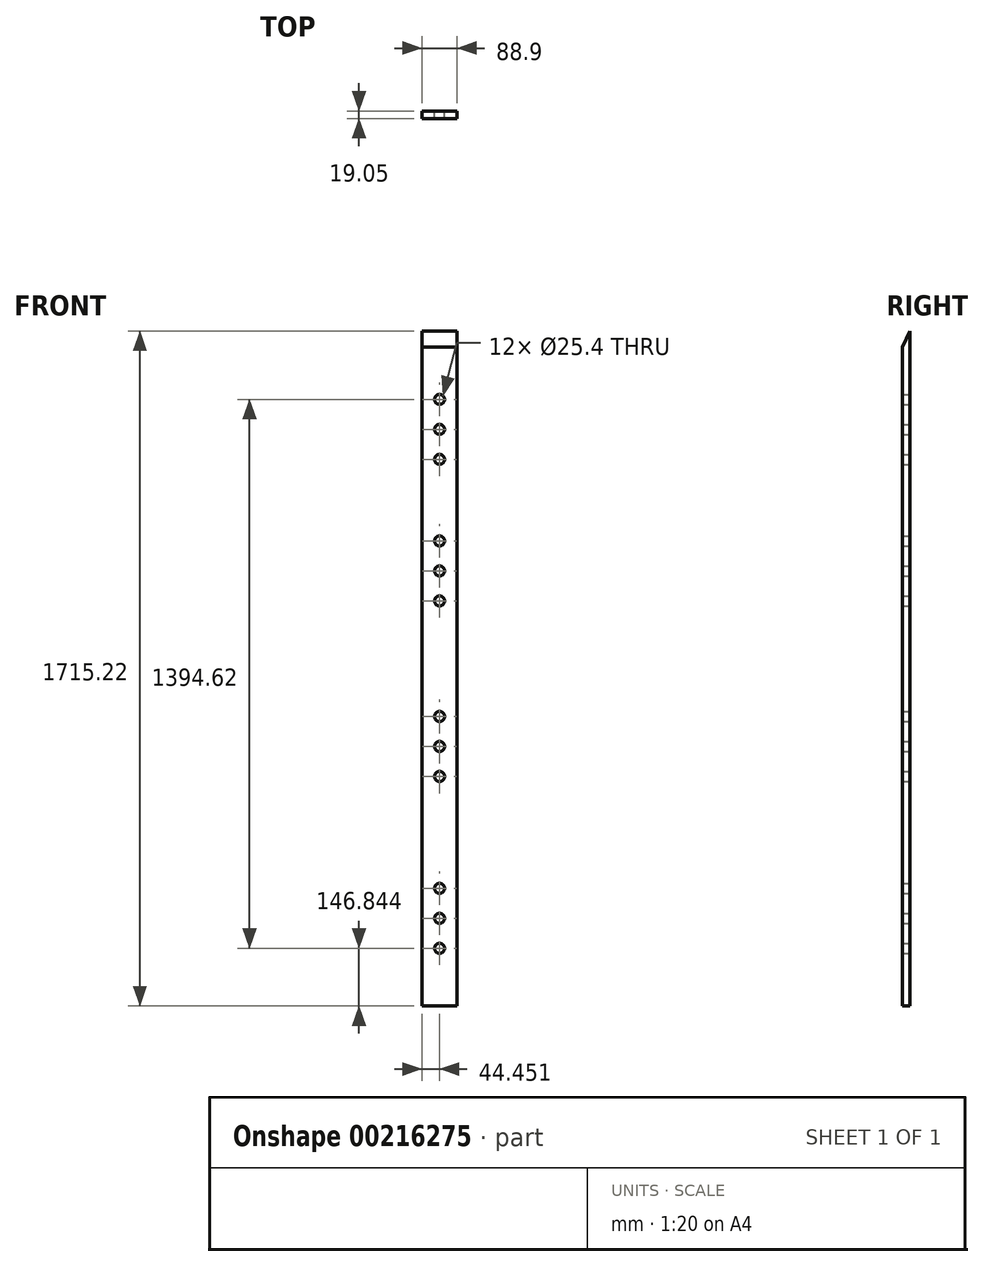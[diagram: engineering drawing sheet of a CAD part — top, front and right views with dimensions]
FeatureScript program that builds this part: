
annotation { "Feature Type Name" : "Feature", "Feature Type Description" : "" }
export const myFeature = defineFeature(function(context is Context, id is Id, definition is map)
    precondition{}
    {
        {
            var Q0;
            Q0=qCreatedBy(makeId("Front.planeOp"),FACE);
            var sketch = newSketch(context, id + "F0", { "sketchPlane" : qUnion([Q0])});
            skLineSegment(sketch, "E0", {"start": v(-1432.56, 319.8) * mm, "end": v(-1343.66, 319.8) * mm});
            skLineSegment(sketch, "E1", {"start": v(-1343.66, 319.8) * mm, "end": v(-1343.66, -1395.43) * mm});
            skLineSegment(sketch, "E2", {"start": v(-1343.66, -1395.43) * mm, "end": v(-1432.56, -1395.43) * mm});
            skLineSegment(sketch, "E3", {"start": v(-1432.56, -1395.43) * mm, "end": v(-1432.56, 319.8) * mm});
            skCircle(sketch, "E4", {"center": v(-1388.1, 146.03) * mm, "radius": 12.7 * mm});
            skCircle(sketch, "E5", {"center": v(-1388.1, 69.83) * mm, "radius": 12.7 * mm});
            skCircle(sketch, "E6", {"center": v(-1388.1, -6.37) * mm, "radius": 12.7 * mm});
            skCircle(sketch, "E7", {"center": v(-1388.1, -213.54) * mm, "radius": 12.7 * mm});
            skCircle(sketch, "E8", {"center": v(-1388.1, -289.74) * mm, "radius": 12.7 * mm});
            skCircle(sketch, "E9", {"center": v(-1388.1, -365.94) * mm, "radius": 12.7 * mm});
            skCircle(sketch, "E10", {"center": v(-1388.1, -659.62) * mm, "radius": 12.7 * mm});
            skCircle(sketch, "E11", {"center": v(-1388.1, -735.82) * mm, "radius": 12.7 * mm});
            skCircle(sketch, "E12", {"center": v(-1388.1, -812.02) * mm, "radius": 12.7 * mm});
            skCircle(sketch, "E13", {"center": v(-1388.1, -1096.19) * mm, "radius": 12.7 * mm});
            skCircle(sketch, "E14", {"center": v(-1388.1, -1172.39) * mm, "radius": 12.7 * mm});
            skCircle(sketch, "E15", {"center": v(-1388.1, -1248.59) * mm, "radius": 12.7 * mm});
            skLineSegment(sketch, "E16", {"start": v(-1388.1, 319.8) * mm, "end": v(-1388.1, -1412.78) * mm, "construction": true});
            skPoint(sketch, "E16.endSnap0", {"position": v(-1388.1, -1395.43) * mm});
            skSolve(sketch);
        }
        {
            var Q0;
            Q0=makeQuery(id+"F0.imprint","IMPRINT",FACE,{"disambiguationData":[TD([[makeQuery(id+"F0.imprint","IMPRINT",EDGE,{"derivedFrom":sQuery(id+"F0.wireOp",EDGE,"E0")}),-1.0]])]});
            extrude(context, id + "F1", {"entities" : qUnion([Q0]), "depth" : 19.05 * mm});
        }
        {
            var Q0;
            Q0=makeQuery(id+"F1.opExtrude","SWEPT_FACE",FACE,{"disambiguationData":[OSD([sQuery(id+"F0.wireOp",EDGE,"E3")])]});
            var sketch = newSketch(context, id + "F2", { "sketchPlane" : qUnion([Q0])});
            skLineSegment(sketch, "E17", {"start": v(0, 319.8) * mm, "end": v(19.05, 278.79) * mm});
            skLineSegment(sketch, "E18", {"start": v(19.05, 278.79) * mm, "end": v(19.05, 319.8) * mm});
            skLineSegment(sketch, "E19", {"start": v(19.05, 319.8) * mm, "end": v(0, 319.8) * mm});
            skSolve(sketch);
        }
        {
            var Q0;
            Q0=makeQuery(id+"F2.imprint","IMPRINT",FACE,{"disambiguationData":[TD([[makeQuery(id+"F2.imprint","IMPRINT",EDGE,{"derivedFrom":sQuery(id+"F2.wireOp",EDGE,"E17")}),1.0]])]});
            extrude(context, id + "F3", {"entities" : qUnion([Q0]), "operationType" : NewBodyOperationType.REMOVE, "endBound" : BoundingType.THROUGH_ALL, "oppositeDirection" : true, "depth" : 25.4 * mm});
        }
    });
